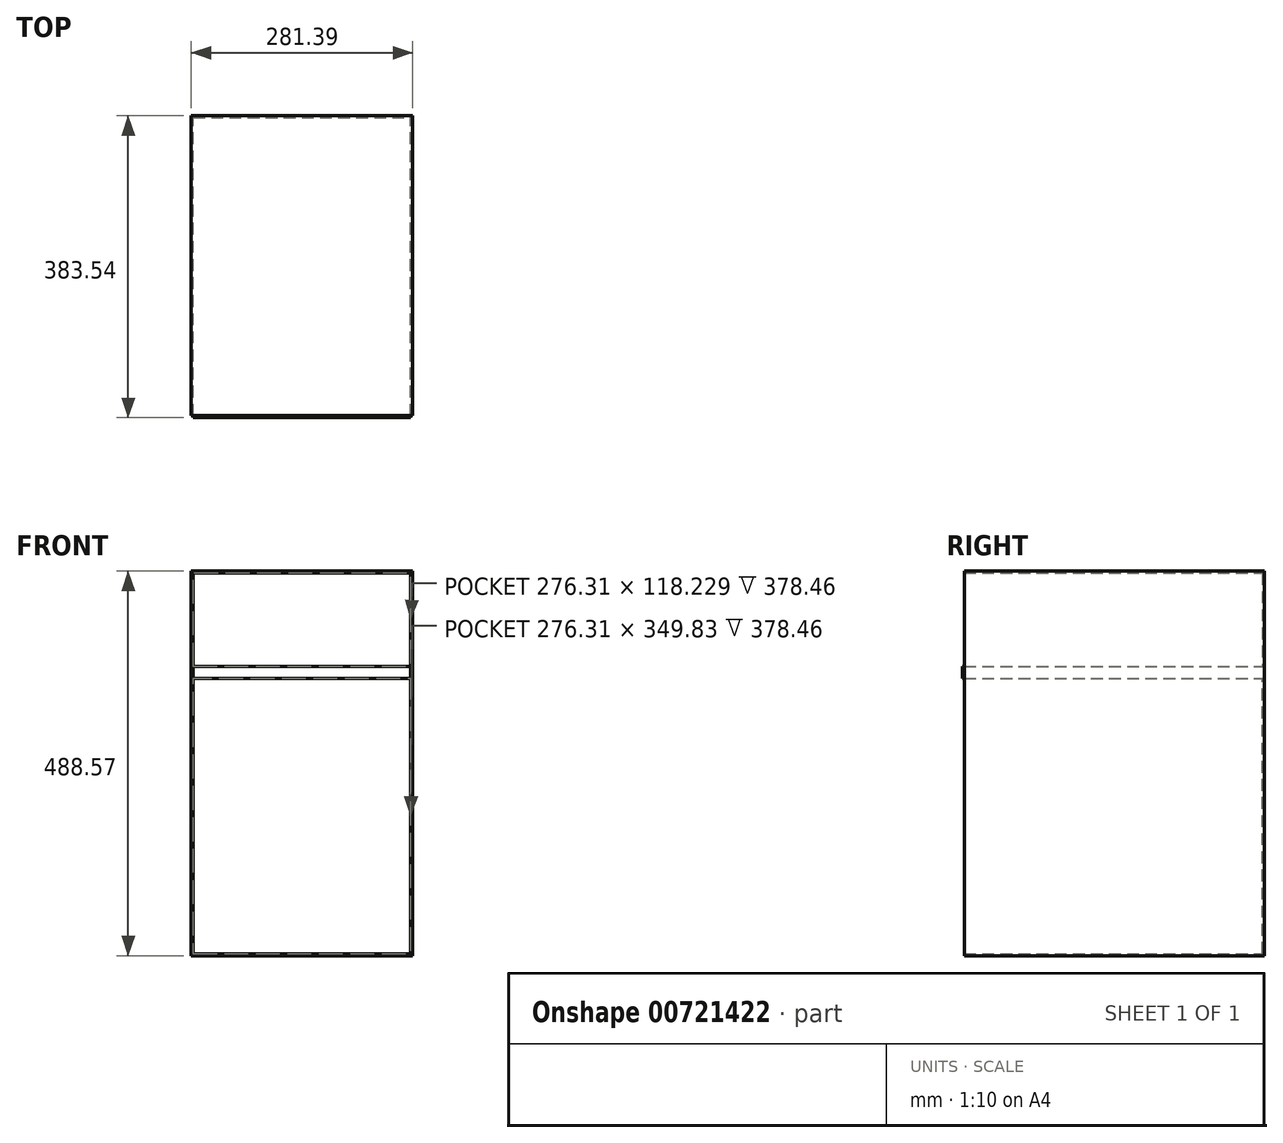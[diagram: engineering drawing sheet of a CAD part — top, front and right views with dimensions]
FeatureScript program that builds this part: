
annotation { "Feature Type Name" : "Feature", "Feature Type Description" : "" }
export const myFeature = defineFeature(function(context is Context, id is Id, definition is map)
    precondition{}
    {
        {
            var Q0;
            Q0=qCreatedBy(makeId("Front.planeOp"),FACE);
            var sketch = newSketch(context, id + "F0", { "sketchPlane" : qUnion([Q0])});
            skLineSegment(sketch, "E0", {"start": v(-186.55, 336.62) * mm, "end": v(94.84, 336.62) * mm});
            skLineSegment(sketch, "E1", {"start": v(-186.55, 336.62) * mm, "end": v(-186.55, -151.95) * mm});
            skLineSegment(sketch, "E2", {"start": v(-186.55, -151.95) * mm, "end": v(94.84, -151.95) * mm});
            skLineSegment(sketch, "E3", {"start": v(94.84, -151.95) * mm, "end": v(94.84, 336.62) * mm});
            skSolve(sketch);
        }
        {
            var Q0;
            Q0 = qSketchRegion(id + "F0", true);
            extrude(context, id + "F1", {"entities" : qUnion([Q0]), "depth" : 381 * mm, "offsetDistance" : 25.4 * mm});
        }
        {
            var Q0;
            Q0=makeQuery(id+"F1.opExtrude","CAP_FACE",FACE,{"disambiguationData":[OSD([sQuery(id+"F0.wireOp",EDGE,"E0"),sQuery(id+"F0.wireOp",EDGE,"E1"),sQuery(id+"F0.wireOp",EDGE,"E2"),sQuery(id+"F0.wireOp",EDGE,"E3")])],"isStart":false});
            shell(context, id + "F2", {"entities" : qUnion([Q0]), "thickness" : 2.54 * mm});
        }
        {
            var Q0;
            Q0=makeQuery(id+"F2.opShell","OFFSET_FACE",FACE,{"disambiguationData":[OSD([sQuery(id+"F0.wireOp",EDGE,"E0"),sQuery(id+"F0.wireOp",EDGE,"E1"),sQuery(id+"F0.wireOp",EDGE,"E2"),sQuery(id+"F0.wireOp",EDGE,"E3")])]});
            var sketch = newSketch(context, id + "F3", { "sketchPlane" : qUnion([Q0])});
            skLineSegment(sketch, "E4", {"start": v(-184, 215.85) * mm, "end": v(92.3, 215.85) * mm});
            skLineSegment(sketch, "E5", {"start": v(-184, 215.85) * mm, "end": v(-184, 200.42) * mm});
            skLineSegment(sketch, "E6", {"start": v(-184, 200.42) * mm, "end": v(92.3, 200.42) * mm});
            skLineSegment(sketch, "E7", {"start": v(92.3, 200.42) * mm, "end": v(92.3, 215.85) * mm});
            skSolve(sketch);
        }
        {
            var Q0;
            Q0 = qSketchRegion(id + "F3", true);
            extrude(context, id + "F4", {"entities" : qUnion([Q0]), "operationType" : NewBodyOperationType.ADD, "depth" : 381 * mm, "offsetDistance" : 25.4 * mm});
        }
    });
